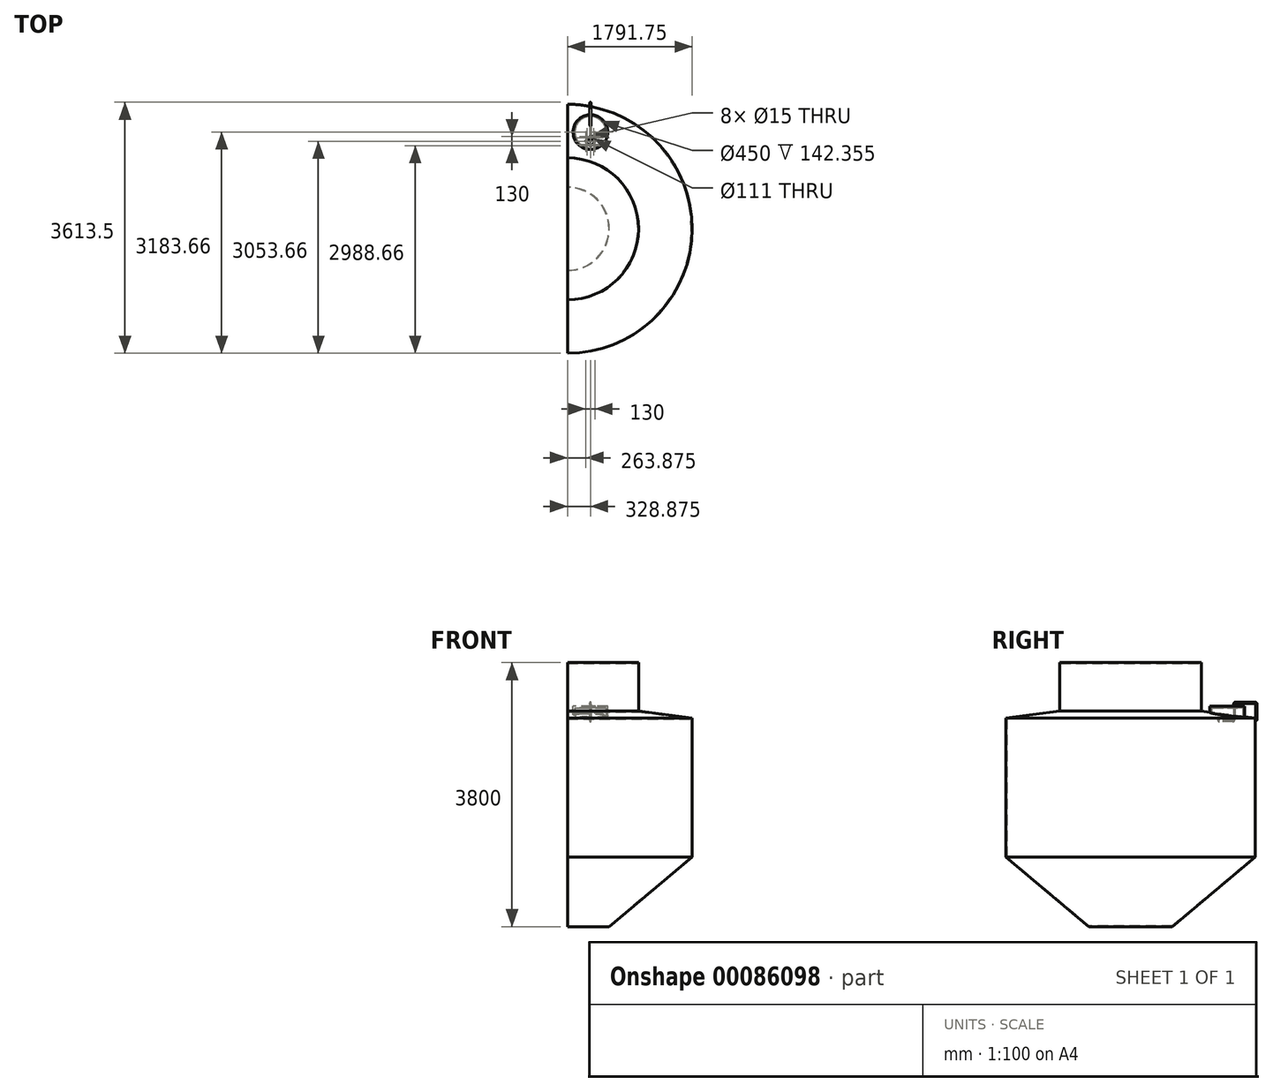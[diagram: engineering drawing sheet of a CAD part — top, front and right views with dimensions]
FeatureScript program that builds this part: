
annotation { "Feature Type Name" : "Feature", "Feature Type Description" : "" }
export const myFeature = defineFeature(function(context is Context, id is Id, definition is map)
    precondition{}
    {
        {
            var Q0;
            Q0=qCreatedBy(makeId("Front.planeOp"),FACE);
            var sketch = newSketch(context, id + "F0", { "sketchPlane" : qUnion([Q0])});
            skLineSegment(sketch, "E0", {"start": v(0, 1900) * mm, "end": v(1021.75, 1900) * mm});
            skLineSegment(sketch, "E1", {"start": v(1021.75, 1900) * mm, "end": v(1021.75, 1200) * mm});
            skLineSegment(sketch, "E2", {"start": v(1021.75, 1200) * mm, "end": v(1791.75, 1100) * mm});
            skLineSegment(sketch, "E3", {"start": v(1791.75, 1100) * mm, "end": v(1791.75, -900) * mm});
            skLineSegment(sketch, "E4", {"start": v(1791.75, -900) * mm, "end": v(600, -1900) * mm});
            skLineSegment(sketch, "E5", {"start": v(600, -1900) * mm, "end": v(0, -1900) * mm});
            skLineSegment(sketch, "E6", {"start": v(0, -1900) * mm, "end": v(0, 1900) * mm});
            skPoint(sketch, "E7", {"position": v(0, 0) * mm});
            skSolve(sketch);
        }
        {
            var Q0;
            Q0=makeQuery(id+"F0.imprint","IMPRINT",FACE,{"disambiguationData":[TD([[makeQuery(id+"F0.imprint","IMPRINT",EDGE,{"derivedFrom":sQuery(id+"F0.wireOp",EDGE,"E0")}),-1.0]])]});
            var Q1;
            Q1=sQuery(id+"F0.wireOp",EDGE,"E6");
            revolve(context, id + "F1", {"entities" : qUnion([Q0]), "axis" : qUnion([Q1]), "revolveType" : RevolveType.SYMMETRIC, "angle" : 180 * degree});
        }
        {
            var Q0;
            Q0=makeQuery(id+"F1.opRevolve","CAP_FACE",FACE,{"disambiguationData":[OSD([sQuery(id+"F0.wireOp",EDGE,"E0"),sQuery(id+"F0.wireOp",EDGE,"E1"),sQuery(id+"F0.wireOp",EDGE,"E2"),sQuery(id+"F0.wireOp",EDGE,"E3"),sQuery(id+"F0.wireOp",EDGE,"E4"),sQuery(id+"F0.wireOp",EDGE,"E5"),sQuery(id+"F0.wireOp",EDGE,"E6")])],"isStart":false});
            shell(context, id + "F2", {"entities" : qUnion([Q0]), "thickness" : 10 * mm});
        }
        {
            var Q0;
            Q0=qCreatedBy(makeId("Top.planeOp"),FACE);
            var Q1;
            Q1=makeQuery(id+"F1.opRevolve","CAP_VERTEX",VERTEX,{"disambiguationData":[OSD([sQuery(id+"F0.wireOp",EDGE,"E2"),sQuery(id+"F0.wireOp",EDGE,"E3")])],"isStart":false});
            cPlane(context, id + "F3", {"entities" : qUnion([Q0, Q1]), "cplaneType" : CPlaneType.PLANE_POINT, "offset" : 150 * mm, "width" : 150 * mm, "height" : 150 * mm});
        }
        {
            var Q0;
            Q0=qCreatedBy(id+"F3.planeOp",FACE);
            var sketch = newSketch(context, id + "F4", { "sketchPlane" : qUnion([Q0])});
            skCircle(sketch, "E8", {"center": v(328.88, 1391.9) * mm, "radius": 225 * mm});
            skSolve(sketch);
        }
        {
            var Q0;
            Q0 = qSketchRegion(id + "F4", true);
            extrude(context, id + "F5", {"entities" : qUnion([Q0]), "operationType" : NewBodyOperationType.REMOVE, "endBound" : BoundingType.THROUGH_ALL, "depth" : 25 * mm});
        }
        {
            var Q0;
            Q0=qCreatedBy(id+"F3.planeOp",FACE);
            cPlane(context, id + "F6", {"entities" : qUnion([Q0]), "cplaneType" : CPlaneType.OFFSET, "offset" : 150 * mm, "width" : 150 * mm, "height" : 150 * mm});
        }
        {
            var Q0;
            Q0=qCreatedBy(id+"F6.planeOp",FACE);
            var sketch = newSketch(context, id + "F7", { "sketchPlane" : qUnion([Q0])});
            skCircle(sketch, "E9.0", {"center": v(328.88, 1391.9) * mm, "radius": 225 * mm});
            skCircle(sketch, "E10", {"center": v(328.88, 1391.9) * mm, "radius": 250 * mm});
            skSolve(sketch);
        }
        {
            var Q0;
            Q0 = qSketchRegion(id + "F7", true);
            extrude(context, id + "F8", {"entities" : qUnion([Q0]), "operationType" : NewBodyOperationType.ADD, "endBound" : BoundingType.UP_TO_NEXT, "oppositeDirection" : true, "depth" : 25 * mm});
        }
        {
            var Q0;
            Q0=makeQuery(id+"F8.opExtrude","CAP_FACE",FACE,{"disambiguationData":[OSD([sQuery(id+"F7.wireOp",EDGE,"E9.0"),sQuery(id+"F7.wireOp",EDGE,"E10")])],"isStart":true});
            var sketch = newSketch(context, id + "F9", { "sketchPlane" : qUnion([Q0])});
            skCircle(sketch, "E11.0", {"center": v(328.88, 1391.9) * mm, "radius": 250 * mm});
            skSolve(sketch);
        }
        {
            var Q0;
            Q0 = qSketchRegion(id + "F9", true);
            extrude(context, id + "F10", {"entities" : qUnion([Q0]), "operationType" : NewBodyOperationType.ADD, "depth" : 20 * mm});
        }
        {
            var Q0;
            Q0=makeQuery(id+"F10.opExtrude","CAP_FACE",FACE,{"disambiguationData":[OSD([sQuery(id+"F9.wireOp",EDGE,"E11.0")])],"isStart":false});
            var sketch = newSketch(context, id + "F11", { "sketchPlane" : qUnion([Q0])});
            skPoint(sketch, "E12", {"position": v(328.88, 1261.9) * mm});
            skCircle(sketch, "E13", {"center": v(263.88, 1261.9) * mm, "radius": 7.5 * mm});
            skCircle(sketch, "E14.1.0", {"center": v(282.91, 1215.94) * mm, "radius": 7.5 * mm});
            skCircle(sketch, "E14.2.0", {"center": v(328.88, 1196.9) * mm, "radius": 7.5 * mm});
            skCircle(sketch, "E14.3.0", {"center": v(374.84, 1215.94) * mm, "radius": 7.5 * mm});
            skCircle(sketch, "E14.4.0", {"center": v(393.88, 1261.9) * mm, "radius": 7.5 * mm});
            skCircle(sketch, "E14.5.0", {"center": v(374.84, 1307.87) * mm, "radius": 7.5 * mm});
            skCircle(sketch, "E14.6.0", {"center": v(328.88, 1326.9) * mm, "radius": 7.5 * mm});
            skCircle(sketch, "E14.7.0", {"center": v(282.91, 1307.87) * mm, "radius": 7.5 * mm});
            skCircle(sketch, "E15", {"center": v(328.88, 1261.9) * mm, "radius": 55.5 * mm});
            skPoint(sketch, "E16", {"position": v(328.88, 1391.9) * mm});
            skSolve(sketch);
        }
        {
            var Q0;
            Q0 = qSketchRegion(id + "F11", true);
            extrude(context, id + "F12", {"entities" : qUnion([Q0]), "operationType" : NewBodyOperationType.REMOVE, "endBound" : BoundingType.UP_TO_NEXT, "oppositeDirection" : true, "depth" : 25 * mm});
        }
        {
            var Q0;
            Q0=qCreatedBy(makeId("Right.planeOp"),FACE);
            var Q1;
            Q1=sQuery(id+"F7.wireOp",VERTEX,"E10.center");
            cPlane(context, id + "F13", {"entities" : qUnion([Q0, Q1]), "cplaneType" : CPlaneType.PLANE_POINT, "offset" : 150 * mm, "width" : 150 * mm, "height" : 150 * mm});
        }
        {
            var Q0;
            Q0=qCreatedBy(id+"F13.planeOp",FACE);
            var sketch = newSketch(context, id + "F14", { "sketchPlane" : qUnion([Q0])});
            skLineSegment(sketch, "E17", {"start": v(1811.75, 1070) * mm, "end": v(1811.75, 1300) * mm});
            skLineSegment(sketch, "E18", {"start": v(1791.75, 1320) * mm, "end": v(1511.75, 1320) * mm});
            skLineSegment(sketch, "E19", {"start": v(1491.75, 1300) * mm, "end": v(1491.75, 1080) * mm});
            skLineSegment(sketch, "E20", {"start": v(1471.75, 1060) * mm, "end": v(1281.9, 1060) * mm});
            skLineSegment(sketch, "E21", {"start": v(1261.9, 1080) * mm, "end": v(1261.9, 1110) * mm});
            skLineSegment(sketch, "E22.0", {"start": v(1206.4, 1270) * mm, "end": v(1317.4, 1270) * mm, "construction": true});
            skPoint(sketch, "E23", {"position": v(1261.9, 1270) * mm});
            skPoint(sketch, "E24.visualSharp", {"position": v(1811.75, 1320) * mm});
            skArc(sketch, "E24.filletArc", {"start": v(1811.75, 1300) * mm, "mid": v(1805.9, 1314.14) * mm, "end": v(1791.75, 1320) * mm});
            skPoint(sketch, "E25.visualSharp", {"position": v(1491.75, 1320) * mm});
            skArc(sketch, "E25.filletArc", {"start": v(1511.75, 1320) * mm, "mid": v(1497.61, 1314.14) * mm, "end": v(1491.75, 1300) * mm});
            skPoint(sketch, "E26.visualSharp", {"position": v(1491.75, 1060) * mm});
            skArc(sketch, "E26.filletArc", {"start": v(1471.75, 1060) * mm, "mid": v(1485.9, 1065.86) * mm, "end": v(1491.75, 1080) * mm});
            skPoint(sketch, "E27.visualSharp", {"position": v(1261.9, 1060) * mm});
            skArc(sketch, "E27.filletArc", {"start": v(1261.9, 1080) * mm, "mid": v(1267.76, 1065.86) * mm, "end": v(1281.9, 1060) * mm});
            skSolve(sketch);
        }
        {
            var Q0;
            Q0=qCreatedBy(makeId("Top.planeOp"),FACE);
            var Q1;
            Q1=sQuery(id+"F14.wireOp",VERTEX,"E17.start");
            cPlane(context, id + "F15", {"entities" : qUnion([Q0, Q1]), "cplaneType" : CPlaneType.PLANE_POINT, "offset" : 150 * mm, "width" : 150 * mm, "height" : 150 * mm});
        }
        {
            var Q0;
            Q0=qCreatedBy(id+"F15.planeOp",FACE);
            var sketch = newSketch(context, id + "F16", { "sketchPlane" : qUnion([Q0])});
            skCircle(sketch, "E28", {"center": v(328.88, 1811.75) * mm, "radius": 10 * mm});
            skSolve(sketch);
        }
        {
            var Q0;
            Q0 = qSketchRegion(id + "F16", true);
            var Q1;
            Q1 = qConstructionFilter(qBodyType(qCreatedBy(id + "F14" ,EDGE), BodyType.WIRE), ConstructionObject.NO);
            sweep(context, id + "F17", {"operationType" : NewBodyOperationType.ADD, "profiles" : qUnion([Q0]), "path" : qUnion([Q1])});
        }
    });
